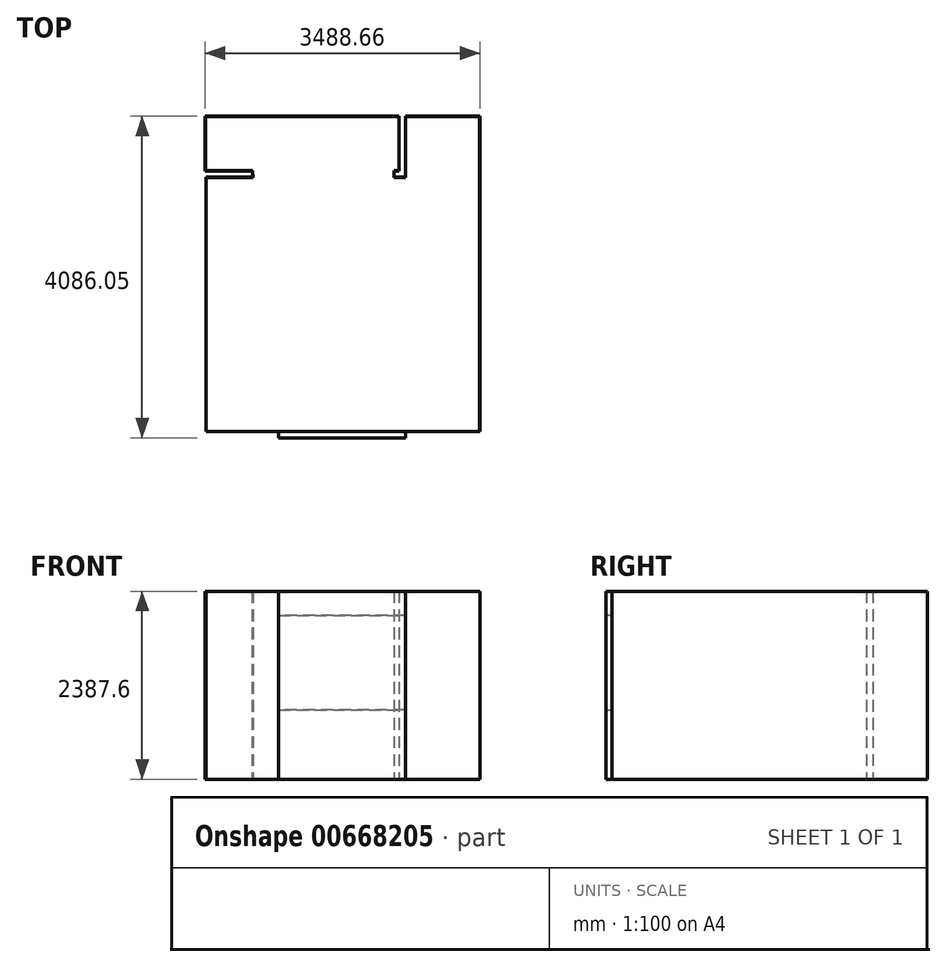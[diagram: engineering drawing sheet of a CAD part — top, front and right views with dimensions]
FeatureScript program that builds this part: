
annotation { "Feature Type Name" : "Feature", "Feature Type Description" : "" }
export const myFeature = defineFeature(function(context is Context, id is Id, definition is map)
    precondition{}
    {
        {
            var Q0;
            Q0=qCreatedBy(makeId("Top.planeOp"),FACE);
            var sketch = newSketch(context, id + "F0", { "sketchPlane" : qUnion([Q0])});
            skLineSegment(sketch, "E0", {"start": v(0, 0) * mm, "end": v(943.93, 0) * mm});
            skLineSegment(sketch, "E1", {"start": v(0, 0) * mm, "end": v(88.81, 0) * mm});
            skLineSegment(sketch, "E2", {"start": v(943.93, 0) * mm, "end": v(853.39, 0) * mm});
            skLineSegment(sketch, "E3", {"start": v(0, 0) * mm, "end": v(0, -776.16) * mm});
            skLineSegment(sketch, "E4", {"start": v(0, -776.16) * mm, "end": v(-143.7, -776.16) * mm});
            skLineSegment(sketch, "E5", {"start": v(-1938.24, -776.16) * mm, "end": v(-2536.42, -776.16) * mm});
            skLineSegment(sketch, "E6", {"start": v(-2536.42, -776.16) * mm, "end": v(-2536.42, -4006.35) * mm});
            skLineSegment(sketch, "E7", {"start": v(943.93, 0) * mm, "end": v(943.93, -4006.35) * mm});
            skLineSegment(sketch, "E8", {"start": v(-2536.42, -4006.35) * mm, "end": v(943.93, -4006.35) * mm});
            skLineSegment(sketch, "E9", {"start": v(-2536.42, -4006.35) * mm, "end": v(-1613.27, -4006.35) * mm});
            skLineSegment(sketch, "E10", {"start": v(943.93, -4006.35) * mm, "end": v(0, -4006.35) * mm});
            skLineSegment(sketch, "E11", {"start": v(-1938.24, -776.16) * mm, "end": v(-1947.53, -695.89) * mm});
            skLineSegment(sketch, "E12", {"start": v(-1947.53, -695.89) * mm, "end": v(-2544.73, -695.89) * mm});
            skLineSegment(sketch, "E13", {"start": v(-2544.73, -695.89) * mm, "end": v(-2544.73, 0) * mm});
            skLineSegment(sketch, "E14", {"start": v(-143.7, -776.16) * mm, "end": v(-143.7, -694.54) * mm});
            skLineSegment(sketch, "E15", {"start": v(-143.7, -694.54) * mm, "end": v(-82.61, -694.54) * mm});
            skLineSegment(sketch, "E16", {"start": v(-82.61, -694.54) * mm, "end": v(-82.61, 0) * mm});
            skLineSegment(sketch, "E17", {"start": v(-82.61, 0) * mm, "end": v(-2544.73, 0) * mm});
            skLineSegment(sketch, "E18", {"start": v(-1613.27, -4006.35) * mm, "end": v(-1613.27, -4086.05) * mm});
            skLineSegment(sketch, "E19", {"start": v(-1613.27, -4086.05) * mm, "end": v(0, -4086.05) * mm});
            skLineSegment(sketch, "E20", {"start": v(0, -4086.05) * mm, "end": v(0, -4006.35) * mm});
            skSolve(sketch);
        }
        {
            var Q0;
            Q0=makeQuery(id+"F0.imprint","IMPRINT",FACE,{"disambiguationData":[TD([[makeQuery(id+"F0.imprint","IMPRINT",EDGE,{"derivedFrom":sQuery(id+"F0.wireOp",EDGE,"E0")}),-1.0]])]});
            var Q1;
            Q1=makeQuery(id+"F0.imprint","IMPRINT",FACE,{"disambiguationData":[TD([[makeQuery(id+"F0.imprint","IMPRINT",EDGE,{"derivedFrom":sQuery(id+"F0.wireOp",EDGE,"E8")}),-1.0]])]});
            extrude(context, id + "F1", {"entities" : qUnion([Q0, Q1]), "depth" : 2387.6 * mm, "offsetDistance" : 25.4 * mm});
        }
        {
            var Q0;
            Q0=makeQuery(id+"F1.opExtrude","CAP_FACE",FACE,{"disambiguationData":[OSD([sQuery(id+"F0.wireOp",EDGE,"E0"),sQuery(id+"F0.wireOp",EDGE,"E1"),sQuery(id+"F0.wireOp",EDGE,"E2"),sQuery(id+"F0.wireOp",EDGE,"E3"),sQuery(id+"F0.wireOp",EDGE,"E4"),sQuery(id+"F0.wireOp",EDGE,"E5"),sQuery(id+"F0.wireOp",EDGE,"E6"),sQuery(id+"F0.wireOp",EDGE,"E7"),sQuery(id+"F0.wireOp",EDGE,"E9"),sQuery(id+"F0.wireOp",EDGE,"E10"),sQuery(id+"F0.wireOp",EDGE,"E11"),sQuery(id+"F0.wireOp",EDGE,"E12"),sQuery(id+"F0.wireOp",EDGE,"E13"),sQuery(id+"F0.wireOp",EDGE,"E14"),sQuery(id+"F0.wireOp",EDGE,"E15"),sQuery(id+"F0.wireOp",EDGE,"E16"),sQuery(id+"F0.wireOp",EDGE,"E17"),sQuery(id+"F0.wireOp",EDGE,"E18"),sQuery(id+"F0.wireOp",EDGE,"E19"),sQuery(id+"F0.wireOp",EDGE,"E20")])],"isStart":false});
            shell(context, id + "F2", {"entities" : qUnion([Q0]), "thickness" : 2.54 * mm});
        }
        {
            var Q0;
            Q0=makeQuery(id+"F1.opExtrude","SWEPT_FACE",FACE,{"disambiguationData":[OSD([sQuery(id+"F0.wireOp",EDGE,"E19")])]});
            var sketch = newSketch(context, id + "F3", { "sketchPlane" : qUnion([Q0])});
            skLineSegment(sketch, "E21", {"start": v(-1613.27, 0) * mm, "end": v(-1613.27, 884.07) * mm});
            skLineSegment(sketch, "E22", {"start": v(-1613.27, 884.07) * mm, "end": v(0, 884.07) * mm});
            skLineSegment(sketch, "E23", {"start": v(0, 884.07) * mm, "end": v(0, 0) * mm});
            skLineSegment(sketch, "E24", {"start": v(0, 0) * mm, "end": v(-1613.27, 0) * mm});
            skLineSegment(sketch, "E25", {"start": v(0, 2387.6) * mm, "end": v(0, 2078.83) * mm});
            skLineSegment(sketch, "E26", {"start": v(0, 2078.83) * mm, "end": v(-1613.27, 2078.83) * mm});
            skLineSegment(sketch, "E27", {"start": v(-1613.27, 2078.83) * mm, "end": v(-1613.27, 2387.6) * mm});
            skLineSegment(sketch, "E28", {"start": v(-1613.27, 2387.6) * mm, "end": v(0, 2387.6) * mm});
            skSolve(sketch);
        }
        {
            var Q0;
            Q0=makeQuery(id+"F3.imprint","IMPRINT",FACE,{"disambiguationData":[TD([[makeQuery(id+"F3.imprint","IMPRINT",EDGE,{"derivedFrom":sQuery(id+"F3.wireOp",EDGE,"E25")}),-1.0]])]});
            var Q1;
            Q1=makeQuery(id+"F3.imprint","IMPRINT",FACE,{"disambiguationData":[TD([[makeQuery(id+"F3.imprint","IMPRINT",EDGE,{"derivedFrom":sQuery(id+"F3.wireOp",EDGE,"E21")}),1.0]])]});
            extrude(context, id + "F4", {"entities" : qUnion([Q0, Q1]), "operationType" : NewBodyOperationType.ADD, "oppositeDirection" : true, "depth" : 83.82 * mm, "offsetDistance" : 25.4 * mm});
        }
    });
